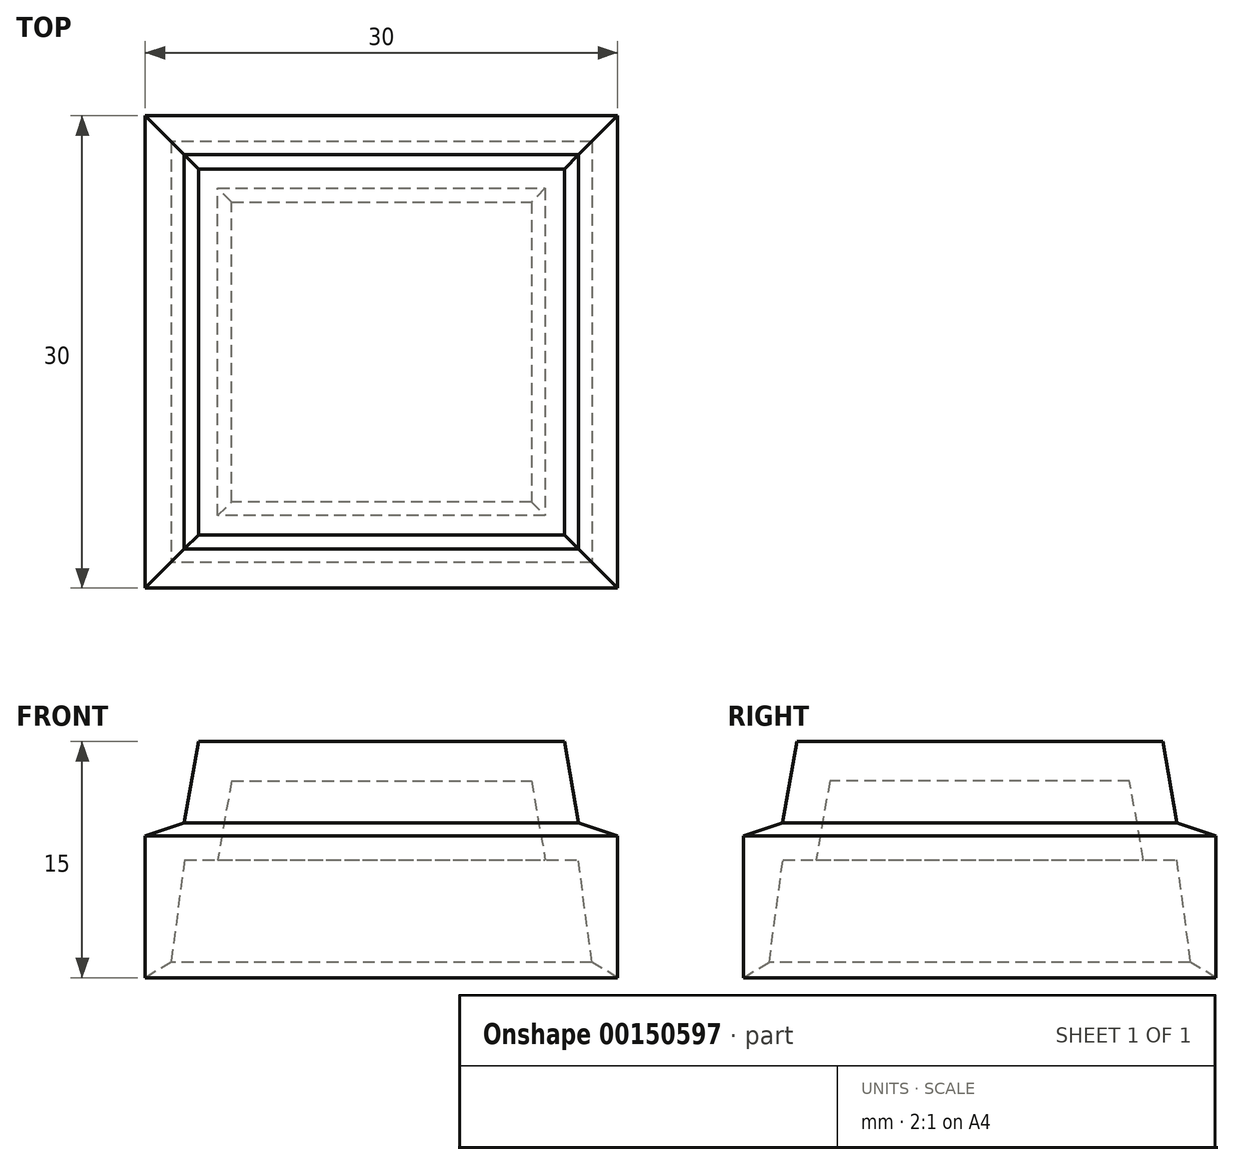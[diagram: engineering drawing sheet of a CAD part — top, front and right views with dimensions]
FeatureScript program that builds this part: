
annotation { "Feature Type Name" : "Feature", "Feature Type Description" : "" }
export const myFeature = defineFeature(function(context is Context, id is Id, definition is map)
    precondition{}
    {
        {
            var Q0;
            Q0=qCreatedBy(makeId("Top.planeOp"),FACE);
            var sketch = newSketch(context, id + "F0", { "sketchPlane" : qUnion([Q0])});
            skLineSegment(sketch, "E0.bottom", {"start": v(0, 0) * mm, "end": v(30, 0) * mm});
            skLineSegment(sketch, "E0.top", {"start": v(0, 30) * mm, "end": v(30, 30) * mm});
            skLineSegment(sketch, "E0.left", {"start": v(0, 0) * mm, "end": v(0, 30) * mm});
            skLineSegment(sketch, "E0.right", {"start": v(30, 0) * mm, "end": v(30, 30) * mm});
            skSolve(sketch);
        }
        {
            var Q0;
            Q0 = qSketchRegion(id + "F0", true);
            extrude(context, id + "F1", {"entities" : qUnion([Q0]), "depth" : 10 * mm});
        }
        {
            var Q0;
            Q0=makeQuery(id+"F1.opExtrude","CAP_FACE",FACE,{"disambiguationData":[OSD([sQuery(id+"F0.wireOp",EDGE,"E0.bottom"),sQuery(id+"F0.wireOp",EDGE,"E0.top"),sQuery(id+"F0.wireOp",EDGE,"E0.left"),sQuery(id+"F0.wireOp",EDGE,"E0.right")])],"isStart":true});
            shell(context, id + "F2", {"entities" : qUnion([Q0]), "thickness" : 2.5 * mm});
        }
        {
            var Q0;
            {var subQ0=sQuery(id+"F0.wireOp",EDGE,"E0.right");Q0=makeQuery(id+"F2.opShell","OFFSET_EDGE",EDGE,{"disambiguationData":[OSD([subQ0]),TDD([makeQuery(id+"F1.opExtrude","CAP_EDGE",EDGE,{"disambiguationData":[OSD([subQ0])],"isStart":true})])]});}
            var Q1;
            {var subQ0=sQuery(id+"F0.wireOp",EDGE,"E0.top");Q1=makeQuery(id+"F2.opShell","OFFSET_EDGE",EDGE,{"disambiguationData":[OSD([subQ0]),TDD([makeQuery(id+"F1.opExtrude","CAP_EDGE",EDGE,{"disambiguationData":[OSD([subQ0])],"isStart":true})])]});}
            var Q2;
            {var subQ0=sQuery(id+"F0.wireOp",EDGE,"E0.left");Q2=makeQuery(id+"F2.opShell","OFFSET_EDGE",EDGE,{"disambiguationData":[OSD([subQ0]),TDD([makeQuery(id+"F1.opExtrude","CAP_EDGE",EDGE,{"disambiguationData":[OSD([subQ0])],"isStart":true})])]});}
            var Q3;
            {var subQ0=sQuery(id+"F0.wireOp",EDGE,"E0.bottom");Q3=makeQuery(id+"F2.opShell","OFFSET_EDGE",EDGE,{"disambiguationData":[OSD([subQ0]),TDD([makeQuery(id+"F1.opExtrude","CAP_EDGE",EDGE,{"disambiguationData":[OSD([subQ0])],"isStart":true})])]});}
            chamfer(context, id + "F3", {"entities" : qUnion([Q0, Q1, Q2, Q3]), "chamferType" : ChamferType.TWO_OFFSETS, "width1" : 1 * mm, "oppositeDirection" : false, "width2" : 7.5 * mm, "tangentPropagation" : true});
        }
        {
            var Q0;
            Q0=makeQuery(id+"F1.opExtrude","CAP_FACE",FACE,{"disambiguationData":[OSD([sQuery(id+"F0.wireOp",EDGE,"E0.bottom"),sQuery(id+"F0.wireOp",EDGE,"E0.top"),sQuery(id+"F0.wireOp",EDGE,"E0.left"),sQuery(id+"F0.wireOp",EDGE,"E0.right")])],"isStart":false});
            var sketch = newSketch(context, id + "F4", { "sketchPlane" : qUnion([Q0])});
            skLineSegment(sketch, "E1.bottom", {"start": v(27.5, 27.5) * mm, "end": v(2.5, 27.5) * mm});
            skLineSegment(sketch, "E1.top", {"start": v(27.5, 2.5) * mm, "end": v(2.5, 2.5) * mm});
            skLineSegment(sketch, "E1.left", {"start": v(27.5, 27.5) * mm, "end": v(27.5, 2.5) * mm});
            skLineSegment(sketch, "E1.right", {"start": v(2.5, 27.5) * mm, "end": v(2.5, 2.5) * mm});
            skPoint(sketch, "E2", {"position": v(15, 0) * mm});
            skPoint(sketch, "E3", {"position": v(30, 15) * mm});
            skPoint(sketch, "E4", {"position": v(15, 2.5) * mm});
            skPoint(sketch, "E5", {"position": v(27.5, 15) * mm});
            skSolve(sketch);
        }
        {
            var Q0;
            Q0 = qSketchRegion(id + "F4", true);
            extrude(context, id + "F5", {"entities" : qUnion([Q0]), "operationType" : NewBodyOperationType.ADD, "depth" : 5 * mm, "hasDraft" : true, "draftAngle" : 10 * degree, "draftPullDirection" : true});
        }
        {
            var Q0;
            Q0=makeQuery(id+"F2.opShell","OFFSET_FACE",FACE,{"disambiguationData":[OSD([sQuery(id+"F0.wireOp",EDGE,"E0.bottom"),sQuery(id+"F0.wireOp",EDGE,"E0.top"),sQuery(id+"F0.wireOp",EDGE,"E0.left"),sQuery(id+"F0.wireOp",EDGE,"E0.right")])]});
            shell(context, id + "F6", {"entities" : qUnion([Q0]), "thickness" : 2.5 * mm});
        }
        {
            var Q0;
            Q0=makeQuery(id+"F1.opExtrude","CAP_EDGE",EDGE,{"disambiguationData":[OSD([sQuery(id+"F0.wireOp",EDGE,"E0.right")])],"isStart":false});
            var Q1;
            Q1=makeQuery(id+"F1.opExtrude","CAP_EDGE",EDGE,{"disambiguationData":[OSD([sQuery(id+"F0.wireOp",EDGE,"E0.bottom")])],"isStart":false});
            var Q2;
            Q2=makeQuery(id+"F1.opExtrude","CAP_EDGE",EDGE,{"disambiguationData":[OSD([sQuery(id+"F0.wireOp",EDGE,"E0.left")])],"isStart":false});
            var Q3;
            Q3=makeQuery(id+"F1.opExtrude","CAP_EDGE",EDGE,{"disambiguationData":[OSD([sQuery(id+"F0.wireOp",EDGE,"E0.top")])],"isStart":false});
            chamfer(context, id + "F7", {"entities" : qUnion([Q0, Q1, Q2, Q3]), "chamferType" : ChamferType.TWO_OFFSETS, "width1" : 1 * mm, "oppositeDirection" : true, "width2" : 3 * mm, "tangentPropagation" : true});
        }
        {
            var Q0;
            {var subQ0=sQuery(id+"F0.wireOp",EDGE,"E0.right");Q0=makeQuery(id+"F3.opChamfer","BLEND_EDGE",EDGE,{"blendedFrom":[makeQuery(id+"F2.opShell","OFFSET_EDGE",EDGE,{"disambiguationData":[OSD([subQ0]),TDD([makeQuery(id+"F1.opExtrude","CAP_EDGE",EDGE,{"disambiguationData":[OSD([subQ0])],"isStart":true})])]}),makeQuery(id+"F1.opExtrude","CAP_FACE",FACE,{"disambiguationData":[OSD([sQuery(id+"F0.wireOp",EDGE,"E0.bottom"),sQuery(id+"F0.wireOp",EDGE,"E0.top"),sQuery(id+"F0.wireOp",EDGE,"E0.left"),subQ0])],"isStart":true})],"blendedInto":[makeQuery(id+"F1.opExtrude","CAP_FACE",FACE,{"disambiguationData":[OSD([sQuery(id+"F0.wireOp",EDGE,"E0.bottom"),sQuery(id+"F0.wireOp",EDGE,"E0.top"),sQuery(id+"F0.wireOp",EDGE,"E0.left"),subQ0])],"isStart":true})]});}
            var Q1;
            {var subQ0=sQuery(id+"F0.wireOp",EDGE,"E0.bottom");Q1=makeQuery(id+"F3.opChamfer","BLEND_EDGE",EDGE,{"blendedFrom":[makeQuery(id+"F2.opShell","OFFSET_EDGE",EDGE,{"disambiguationData":[OSD([subQ0]),TDD([makeQuery(id+"F1.opExtrude","CAP_EDGE",EDGE,{"disambiguationData":[OSD([subQ0])],"isStart":true})])]}),makeQuery(id+"F1.opExtrude","CAP_FACE",FACE,{"disambiguationData":[OSD([subQ0,sQuery(id+"F0.wireOp",EDGE,"E0.top"),sQuery(id+"F0.wireOp",EDGE,"E0.left"),sQuery(id+"F0.wireOp",EDGE,"E0.right")])],"isStart":true})],"blendedInto":[makeQuery(id+"F1.opExtrude","CAP_FACE",FACE,{"disambiguationData":[OSD([subQ0,sQuery(id+"F0.wireOp",EDGE,"E0.top"),sQuery(id+"F0.wireOp",EDGE,"E0.left"),sQuery(id+"F0.wireOp",EDGE,"E0.right")])],"isStart":true})]});}
            var Q2;
            {var subQ0=sQuery(id+"F0.wireOp",EDGE,"E0.top");Q2=makeQuery(id+"F3.opChamfer","BLEND_EDGE",EDGE,{"blendedFrom":[makeQuery(id+"F2.opShell","OFFSET_EDGE",EDGE,{"disambiguationData":[OSD([subQ0]),TDD([makeQuery(id+"F1.opExtrude","CAP_EDGE",EDGE,{"disambiguationData":[OSD([subQ0])],"isStart":true})])]}),makeQuery(id+"F1.opExtrude","CAP_FACE",FACE,{"disambiguationData":[OSD([sQuery(id+"F0.wireOp",EDGE,"E0.bottom"),subQ0,sQuery(id+"F0.wireOp",EDGE,"E0.left"),sQuery(id+"F0.wireOp",EDGE,"E0.right")])],"isStart":true})],"blendedInto":[makeQuery(id+"F1.opExtrude","CAP_FACE",FACE,{"disambiguationData":[OSD([sQuery(id+"F0.wireOp",EDGE,"E0.bottom"),subQ0,sQuery(id+"F0.wireOp",EDGE,"E0.left"),sQuery(id+"F0.wireOp",EDGE,"E0.right")])],"isStart":true})]});}
            var Q3;
            {var subQ0=sQuery(id+"F0.wireOp",EDGE,"E0.left");Q3=makeQuery(id+"F3.opChamfer","BLEND_EDGE",EDGE,{"blendedFrom":[makeQuery(id+"F2.opShell","OFFSET_EDGE",EDGE,{"disambiguationData":[OSD([subQ0]),TDD([makeQuery(id+"F1.opExtrude","CAP_EDGE",EDGE,{"disambiguationData":[OSD([subQ0])],"isStart":true})])]}),makeQuery(id+"F1.opExtrude","CAP_FACE",FACE,{"disambiguationData":[OSD([sQuery(id+"F0.wireOp",EDGE,"E0.bottom"),sQuery(id+"F0.wireOp",EDGE,"E0.top"),subQ0,sQuery(id+"F0.wireOp",EDGE,"E0.right")])],"isStart":true})],"blendedInto":[makeQuery(id+"F1.opExtrude","CAP_FACE",FACE,{"disambiguationData":[OSD([sQuery(id+"F0.wireOp",EDGE,"E0.bottom"),sQuery(id+"F0.wireOp",EDGE,"E0.top"),subQ0,sQuery(id+"F0.wireOp",EDGE,"E0.right")])],"isStart":true})]});}
            chamfer(context, id + "F8", {"entities" : qUnion([Q0, Q1, Q2, Q3]), "chamferType" : ChamferType.TWO_OFFSETS, "width1" : 1 * mm, "oppositeDirection" : true, "width2" : 1.5 * mm, "tangentPropagation" : true});
        }
    });
